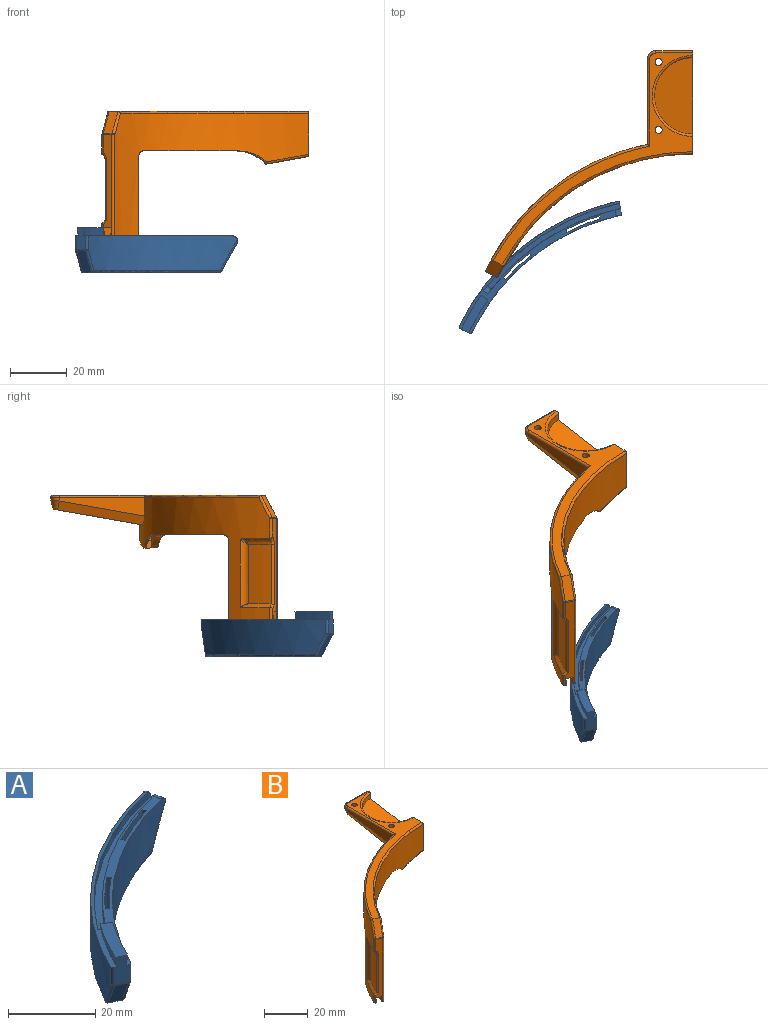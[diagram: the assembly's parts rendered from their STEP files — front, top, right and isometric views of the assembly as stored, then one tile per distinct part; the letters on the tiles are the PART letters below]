
ASSEMBLY  parts=2 mates=1
PART A: 35 faces, bbox 66.2x54x35.7 mm
  f0: plane 55.46x46.32mm, normal (0,0,1), area 192.5mm2, adj f1,f2,f3,f4,f5,f6,f7,f9
  f1: plane 13x0.74mm, normal (0.67,0.74,0), area 13mm2, adj f0,f2,f12,f13,f25
  f2: cylinder r=77.7mm len=13mm, axis (0,0,1), area 162.8mm2, adj f0,f1,f3,f13
  f3: plane 13x0.78mm, normal (-0.78,-0.62,0), area 13mm2, adj f0,f2,f12,f13,f25
  f4: plane 13x0.89mm, normal (0.89,0.46,0), area 13mm2, adj f0,f5,f10,f13,f25
  f5: cylinder r=77.7mm len=13mm, axis (0,0,1), area 167.9mm2, adj f0,f4,f6,f13
  f6: plane 13x0.95mm, normal (-0.95,-0.3,0), area 13mm2, adj f0,f5,f10,f13,f25
  f7: cylinder r=76mm len=52.67mm, axis (0,0,1), area 794.7mm2, adj f0,f23,f24,f25,f26,f27
  f8: plane 10x6.24mm, normal (0.85,0.16,-0.5), area 39.4mm2, adj f13,f23,f24,f25,f29
  f9: cylinder r=81mm len=56.24mm, axis (0,0,1), area 850.7mm2, adj f0,f23,f29,f30,f32,f34
  f10: cylinder r=76.7mm len=12.99mm, axis (0,0,1), area 165.7mm2, adj f0,f4,f6,f25
  f11: plane 7.61x3.08mm, normal (-0.42,-0.91,0), area 23.5mm2, adj f0,f18,f19,f20,f26,f30,f31
  f12: cylinder r=76.7mm len=12.99mm, axis (0,0,1), area 160.7mm2, adj f0,f1,f3,f25
  f13: plane 48.86x40.3mm, normal (0,0,-1), area 187.9mm2, adj f1,f2,f3,f4,f5,f6,f8,f22
  f14: cylinder r=78.3mm len=46.91mm, axis (0,0,1), area 110mm2, adj f0,f16,f17,f23
  f15: cylinder r=80.2mm len=48.08mm, axis (0,0,1), area 112.8mm2, adj f0,f16,f17,f23
  f16: plane 47.23x30.4mm, normal (0,0,1), area 105.8mm2, adj f14,f15,f17,f23
  f17: cylinder r=2mm len=2.75mm, axis (0.8,-0.59,0), area 6mm2, adj f0,f14,f15,f16
  f18: cone r=79.5mm half-angle=8.6deg, axis (0,0,1), area 39.8mm2, adj f0,f11,f20,f21
  f19: cone r=77mm half-angle=8.6deg, axis (0,0,-1), area 38.5mm2, adj f0,f11,f20,f21
  f20: plane 13.34x9.45mm, normal (0,0,1), area 41.1mm2, adj f11,f18,f19,f21
  f21: plane 2.82x2.45mm, normal (0.58,0.82,0), area 7.3mm2, adj f0,f18,f19,f20
  f22: plane 7.81x5.46mm, normal (-0.37,-0.78,-0.5), area 30.7mm2, adj f13,f25,f27,f31,f34
  f23: cylinder r=2mm len=5.35mm, axis (0.19,-0.98,0), area 13.5mm2, adj f0,f7,f8,f9,f14,f15,f16,f24
  f24: bspline ~11.77x6.83mm, area 14.6mm2, adj f7,f8,f23,f25
  f25: torus R=76.8mm, axis (0,0,1), area 72.4mm2, adj f1,f3,f4,f6,f7,f8,f10,f12
  f26: cylinder r=0.8mm len=4.79mm, axis (0,0,1), area 6mm2, adj f0,f7,f11,f28
  f27: bspline ~8.22x4.33mm, area 10.8mm2, adj f7,f22,f25,f28
  f28: sphere r=0.8mm, area 0.3mm2, adj f26,f27,f31
  f29: bspline ~30.67x17.88mm, area 16mm2, adj f8,f9,f13,f23,f32
  f30: cylinder r=0.8mm len=4.79mm, axis (0,0,1), area 6.1mm2, adj f0,f9,f11,f33
  f31: cylinder r=0.8mm len=3.12mm, axis (0.91,-0.42,0), area 1.4mm2, adj f11,f22,f28,f33
  f32: torus R=80.2mm, axis (0,0,1), area 79.8mm2, adj f9,f13,f29,f34
  f33: sphere r=0.8mm, area 0.3mm2, adj f30,f31,f34
  f34: bspline ~30.67x16.39mm, area 11.4mm2, adj f9,f13,f22,f32,f33
PART B: 91 faces, bbox 83.4x95.9x66.1 mm
  f0: cylinder r=80mm len=9mm, axis (0,0,-1), area 18mm2, adj f3,f27,f29,f58
  f1: cylinder r=80mm len=45.52mm, axis (0,0,-1), area 452.5mm2, adj f27,f29,f38,f58
  f2: cylinder r=13.5mm len=27mm, axis (0,0,1), area 160.8mm2, adj f3,f53,f54,f66,f67,f89
  f3: plane 36.56x16.06mm, normal (1,0,0), area 132.2mm2, adj f0,f2,f4,f14,f24,f26,f27,f29
  f4: cylinder r=81mm len=72.99mm, axis (0,0,1), area 1324.1mm2, adj f3,f6,f12,f13,f24,f40,f47,f50
  f5: plane 35.79x3.08mm, normal (-0.42,-0.91,0), area 83.2mm2, adj f6,f42,f43,f45,f76,f79,f80,f83
  f6: plane 17.17x13.03mm, normal (0,0,-1), area 51.5mm2, adj f4,f5,f13,f14,f15,f16,f17,f18
  f7: cylinder r=77.7mm len=11mm, axis (0,0,1), area 50.3mm2, adj f8,f11,f19,f29,f36,f38
  f8: plane 10.07x0.78mm, normal (-0.78,-0.62,0), area 5.7mm2, adj f7,f11,f23,f28,f29,f36
  f9: plane 10.07x0.89mm, normal (0.89,0.46,0), area 5.7mm2, adj f11,f20,f22,f28,f29,f37
  f10: plane 10.15x0.95mm, normal (-0.95,-0.3,0), area 5.8mm2, adj f20,f22,f29,f30,f37,f46
  f11: plane 36.03x26.01mm, normal (0,0,-1), area 75.1mm2, adj f7,f8,f9,f14,f16,f19,f20,f22
  f12: plane 37.21x26.05mm, normal (0,0,-1), area 36.3mm2, adj f4,f18,f40,f47
  f13: plane 28x0.63mm, normal (0.61,0.79,0), area 22.4mm2, adj f4,f6,f18,f40
  f14: cylinder r=76mm len=68.47mm, axis (0,0,1), area 1649.8mm2, adj f3,f6,f11,f15,f39,f46,f75,f78
  f15: plane 28x1.82mm, normal (0.61,0.79,0), area 64.4mm2, adj f6,f14,f16,f39
  f16: cylinder r=78.3mm len=48.35mm, axis (0,0,1), area 185.2mm2, adj f6,f11,f15,f17,f21,f25,f39,f41
  f17: plane 30x1.53mm, normal (0.59,0.8,0), area 57mm2, adj f6,f16,f18,f41
  f18: cylinder r=80.2mm len=49.52mm, axis (0,0,1), area 191.1mm2, adj f6,f12,f13,f17,f21,f25,f40,f41
  f19: plane 11x0.74mm, normal (0.67,0.74,0), area 10.3mm2, adj f7,f11,f23,f36
  f20: cylinder r=77.7mm len=11.93mm, axis (0,0,1), area 51.7mm2, adj f9,f10,f11,f29,f46
  f21: plane 2.65x1.87mm, normal (-0.98,-0.19,0), area 5mm2, adj f16,f18,f24,f48
  f22: cylinder r=76.7mm len=11.77mm, axis (0,0,1), area 111.8mm2, adj f9,f10,f11,f37,f46
  f23: cylinder r=76.7mm len=9.02mm, axis (0,0,1), area 108.4mm2, adj f8,f11,f19,f36
  f24: plane 15.16x5.59mm, normal (0.17,0,-0.98), area 63.5mm2, adj f3,f4,f21,f46,f47,f90
  f25: plane 44.76x29.84mm, normal (0,0,-1), area 101mm2, adj f16,f18,f41,f48
  f26: plane 74.97x70.53mm, normal (0,0,1), area 440.5mm2, adj f3,f49,f59,f60,f73,f74,f75,f77
  f27: plane 57.96x28.24mm, normal (0,0,-1), area 180.7mm2, adj f0,f1,f3,f28,f30,f31,f32,f33
  f28: cylinder r=77mm len=12.75mm, axis (0,0,-1), area 136.8mm2, adj f8,f9,f27,f29,f31,f34
  f29: plane 57.96x27.71mm, normal (0,0,1), area 177.7mm2, adj f0,f1,f3,f7,f8,f9,f10,f20
  f30: cylinder r=77mm len=23.35mm, axis (0,0,-1), area 213.5mm2, adj f3,f10,f27,f29,f32
  f31: plane 2.93x0.62mm, normal (-0.89,-0.46,0), area 1.7mm2, adj f27,f28,f33,f37
  f32: plane 2.93x0.67mm, normal (0.95,0.3,0), area 1.7mm2, adj f27,f30,f33,f37
  f33: cylinder r=77.7mm len=11.93mm, axis (0,0,-1), area 25.8mm2, adj f27,f31,f32,f37
  f34: plane 2.93x0.55mm, normal (0.78,0.62,0), area 1.7mm2, adj f27,f28,f35,f36
  f35: cylinder r=77.7mm len=9.12mm, axis (0,0,-1), area 25mm2, adj f27,f34,f36,f38
  f36: torus R=79.7mm, axis (0,0,1), area 31.3mm2, adj f7,f8,f19,f23,f34,f35
  f37: torus R=79.7mm, axis (0,0,1), area 32.3mm2, adj f9,f10,f22,f31,f32,f33
  f38: cylinder r=3mm len=9mm, axis (0,0,-1), area 36.6mm2, adj f1,f7,f27,f29,f35
  f39: cylinder r=2mm len=3.06mm, axis (-0.79,0.61,0), area 7.2mm2, adj f11,f14,f15,f16
  f40: cylinder r=2mm len=2.09mm, axis (-0.79,0.61,0), area 2.5mm2, adj f4,f12,f13,f18
  f41: cylinder r=2mm len=2.75mm, axis (-0.8,0.59,0), area 6mm2, adj f16,f17,f18,f25
  f42: cone r=79.58mm half-angle=8.6deg, axis (0,0,1), area 39.8mm2, adj f5,f6,f44,f45
  f43: cone r=76.92mm half-angle=8.6deg, axis (0,0,-1), area 38.5mm2, adj f5,f6,f44,f45
  f44: plane 2.82x2.58mm, normal (-0.58,-0.82,0), area 7.7mm2, adj f6,f42,f43,f45
  f45: plane 13.43x9.6mm, normal (0,0,-1), area 43.3mm2, adj f5,f42,f43,f44
  f46: bspline ~53.16x20.61mm, area 25.4mm2, adj f10,f11,f14,f16,f20,f22,f24,f90
  f47: bspline ~61x23.06mm, area 9.7mm2, adj f4,f12,f18,f24
  f48: cylinder r=4mm len=4.3mm, axis (0.19,-0.98,0), area 11.9mm2, adj f16,f18,f21,f25
  f49: plane 7.81x5.46mm, normal (-0.37,-0.78,0.5), area 30.7mm2, adj f26,f75,f78,f84,f85
  f50: plane 30.1x6.51mm, normal (-1,0,0), area 116.1mm2, adj f4,f61,f64,f77
  f51: plane 32.65x15.26mm, normal (0,0.17,-0.98), area 453.2mm2, adj f3,f4,f59,f60,f62,f63,f64
  f52: plane 13x0.91mm, normal (0,1,0), area 11.8mm2, adj f3,f61,f62,f73
  f53: plane 28.52x14.81mm, normal (0,-0.17,0.98), area 295mm2, adj f2,f3,f54,f65,f66
  f54: plane 6.65x3.18mm, normal (-1,0,0), area 16.7mm2, adj f2,f53,f55,f57,f58,f65,f67
  f55: plane 6x4.43mm, normal (0,0,-1), area 10.8mm2, adj f54,f56,f58,f67
  f56: cylinder r=2.5mm len=5mm, axis (0,-1,0), area 25.4mm2, adj f55,f57,f58,f66
  f57: plane 6x4.43mm, normal (0,0,1), area 10.8mm2, adj f54,f56,f58,f65
  f58: bspline ~12.99x12.37mm, area 89mm2, adj f0,f1,f27,f29,f54,f55,f56,f57
  f59: cylinder r=1.25mm len=9.65mm, axis (0,0,1), area 74.9mm2, adj f26,f51
  f60: cylinder r=1.25mm len=5.42mm, axis (0,0,1), area 41.7mm2, adj f26,f51
  f61: cylinder r=3mm len=3mm, axis (0,0,-1), area 5mm2, adj f50,f52,f63,f74
  f62: plane 13x3.14mm, normal (0,0.97,-0.24), area 42.1mm2, adj f3,f51,f52,f63
  f63: bspline ~3.43x3mm, area 12.2mm2, adj f51,f61,f62,f64
  f64: plane 30.65x8.5mm, normal (-0.92,0.07,-0.38), area 106.2mm2, adj f4,f50,f51,f63
  f65: cone r=14.5mm half-angle=45deg, axis (0,0,1), area 4.3mm2, adj f53,f54,f57,f66
  f66: bspline ~7x3.87mm, area 9.3mm2, adj f2,f53,f56,f65,f67
  f67: cone r=13.5mm half-angle=45deg, axis (0,0,-1), area 8.7mm2, adj f2,f54,f55,f66
  f68: cylinder r=79.71mm len=21mm, axis (0,0,1), area 195.5mm2, adj f69,f70,f71,f83
  f69: revolved ~10.15x6.53mm, area 27.2mm2, adj f4,f68,f72,f86,f88
  f70: revolved ~10.88x7.01mm, area 20.3mm2, adj f4,f68,f71,f76,f80,f83
  f71: cylinder r=3mm len=23.64mm, axis (0,0,1), area 63.6mm2, adj f4,f68,f70,f72
  f72: bspline ~2.94x2.35mm, area 1.4mm2, adj f4,f69,f71
  f73: cylinder r=0.8mm len=13mm, axis (-1,0,0), area 16.3mm2, adj f3,f26,f52,f74
  f74: torus R=2.2mm, axis (0,0,1), area 5.3mm2, adj f26,f61,f73,f77
  f75: torus R=76.8mm, axis (0,0,1), area 102.6mm2, adj f3,f14,f26,f49,f78
  f76: cylinder r=0.8mm len=4.34mm, axis (0,0,1), area 5.3mm2, adj f4,f5,f6,f70,f80
  f77: cylinder r=0.8mm len=30.75mm, axis (0,-1,0), area 38.2mm2, adj f26,f50,f74,f81
  f78: bspline ~8.22x4.33mm, area 10.8mm2, adj f14,f49,f75,f82
  f79: cylinder r=0.8mm len=35.79mm, axis (0,0,1), area 44.7mm2, adj f5,f6,f14,f82
  f80: bspline ~12.79x11.58mm, area 2.3mm2, adj f5,f70,f76,f83
  f81: torus R=80.2mm, axis (0,0,1), area 88.9mm2, adj f4,f26,f77,f84
  f82: sphere r=0.8mm, area 0.3mm2, adj f78,f79,f85
  f83: cylinder r=0.8mm len=21.33mm, axis (0,0,1), area 26.7mm2, adj f5,f68,f70,f80,f86
  f84: bspline ~30.67x16.39mm, area 11.4mm2, adj f4,f26,f49,f81,f87
  f85: cylinder r=0.8mm len=3.12mm, axis (0.91,-0.42,0), area 1.4mm2, adj f5,f49,f82,f87
  f86: bspline ~3.31x2.25mm, area 3.5mm2, adj f5,f69,f83,f88
  f87: sphere r=0.8mm, area 0.3mm2, adj f84,f85,f88
  f88: cylinder r=0.8mm len=6.97mm, axis (0,0,1), area 8.6mm2, adj f4,f5,f69,f86,f87
  f89: torus R=14.3mm, axis (0,0,1), area 54.4mm2, adj f2,f3,f26
  f90: bspline ~15.05x3.44mm, area 18.5mm2, adj f3,f14,f24,f46
PLACE A t=(15.55,-71.48,11.18)mm
PLACE B t=(24.95,-51.62,11.18)mm
MATE slider B.f5 <-> A.f11  axis (-0.42,-0.91,0) through (-47.55,-38.62,-18)mm
